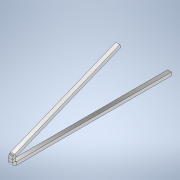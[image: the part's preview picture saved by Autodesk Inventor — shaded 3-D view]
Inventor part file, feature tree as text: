
AUTODESK INVENTOR PART (.ipt)
format: ipt  version: 2020.1 (Build 241239000, 239)  size: 143,360 bytes
history: native  units: mm
features: sheet_metal_op x7, sketch x3, other x3
ambient origin geometry x8: Origin, YZ Plane, XZ Plane, XY Plane, X Axis, Y Axis, Z Axis, Center Point
bodies: Solid1 (feature_tree)
feature tree (13):
  sheet_metal_op  "Face1"
  sheet_metal_op  "Flange1"
  sheet_metal_op  "Flange2"
  sketch  "Sketch1"  dims[d0=0.448mm]
  other  "Plate1"
  sketch  "Sketch2"  dims[d1=17.35mm]
  other  "Plate2"
  sheet_metal_op  "Bend1"
  sheet_metal_op  "Corner1"
  sketch  "Sketch3"  dims[d2=0.35mm d3=0.35mm d4=0.175mm d5=0.7mm d6=0.1mm d7=0.75mm d8=90.0deg d9=0.1mm d10=1.4mm d11=0.35mm d12=0.1mm d13=0.35mm d14=0.175mm d15=0.7mm d16=0.1mm d17=12.95mm d18=11.868239mm d19=0.1mm d20=1.4mm d21=0.35mm d22=0.1mm]
  other  "Plate3"
  sheet_metal_op  "Bend2"
  sheet_metal_op  "Corner2"
